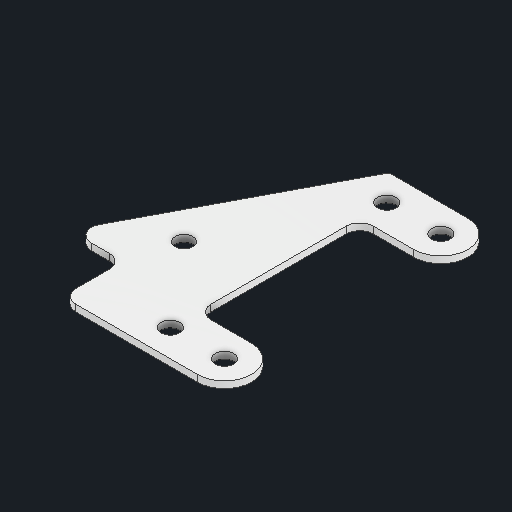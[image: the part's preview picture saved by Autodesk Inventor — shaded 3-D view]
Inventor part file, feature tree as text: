
AUTODESK INVENTOR PART (.ipt)
format: ipt  version: 2025 (Build 290162000, 162)  size: 164,864 bytes
history: native  units: in
note: dims shown in document units (in); Inventor stores cm internally (conversion verified against a paired STEP export)
features: other x5, extrude x1, fillet x1, sketch x1
ambient origin geometry x8: Origin, YZ Plane, XZ Plane, XY Plane, X Axis, Y Axis, Z Axis, Center Point
bodies: Solid1 (feature_tree)
feature tree (8):
  other  "gusset.ipt"
  other  "Blocks"
  extrude  "Extrusion2"  Depth=0.125in
  fillet  "Fillet1"  Radius=0.3937in
  other  "main"
  other  "Solid1::gusset.ipt"
  other  "TaggingFeature1"
  sketch  "Sketch2"  dims[d0=0.125in d3=0.125in d4=0.3937in d5=1.0in d6=0.0in d7=0.125in]
